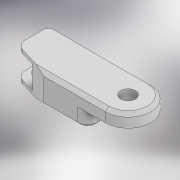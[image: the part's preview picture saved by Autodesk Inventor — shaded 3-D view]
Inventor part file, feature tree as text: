
AUTODESK INVENTOR PART (.ipt)
format: ipt  version: 2022 (Build 260153000, 153)  size: 258,048 bytes
history: native  units: mm
features: extrude x9, sketch x8, projected_geometry x6, fillet x3, chamfer x3
ambient origin geometry x8: Origin, YZ Plane, XZ Plane, XY Plane, X Axis, Y Axis, Z Axis, Center Point
bodies: Solid1 (feature_tree)
feature tree (29):
  sketch  "Sketch2"  dims[d0=4.4mm d1=13.5mm]
  extrude  "Extrusion1"  Depth=13.5mm
  extrude  "Extrusion2"  Depth=8.85mm TaperAngle=0.0deg
  extrude  "Extrusion3"  Depth=1.0mm
  extrude  "Extrusion4"  Depth=8.85mm TaperAngle=0.0deg
  extrude  "Extrusion5"  Depth=8.0mm TaperAngle=0.0deg
  extrude  "Extrusion6"  Depth=8.0mm TaperAngle=0.0deg
  extrude  "Extrusion7"  Depth=3.0mm TaperAngle=0.0deg
  sketch  "Sketch8"  dims[d17=10.25mm d18=0.0mm d19=10.25mm d20=0.0mm d21=3.0mm d22=2.0mm d23=2.0mm d24=45.0deg d25=2.0mm d26=2.0mm d27=45.0deg d28=3.0mm]
  fillet  "Fillet1"  Radius=3.0mm
  chamfer  "Chamfer1"  Distance=2.0mm Angle=45.0deg
  chamfer  "Chamfer2"  Distance=2.0mm Angle=45.0deg
  fillet  "Fillet2"  Radius=3.0mm
  sketch  "Sketch9"  dims[d32=3.85mm d33=0.0mm d34=10.0mm d35=0.0mm d36=1.0mm d37=2.0mm d38=45.0deg d39=1.0mm]
  extrude  "Extrusion8"  Depth=10.0mm TaperAngle=0.0deg
  extrude  "Extrusion9"  Depth=1.0mm TaperAngle=45.0deg
  chamfer  "Chamfer4"  Distance=1.0mm
  fillet  "Fillet3"  [1 undecoded]
  sketch  "Sketch3"  dims[d2=3.85mm d3=0.0mm d4=8.85mm d5=0.0mm]
  projected_geometry  "Projected Loop1"
  sketch  "Sketch4"  dims[d6=0.5mm d7=1.0mm]
  projected_geometry  "Projected Loop2"
  sketch  "Sketch5"  dims[d8=12.5mm d9=8.85mm d10=0.0mm]
  projected_geometry  "Projected Loop3"
  sketch  "Sketch6"  dims[d11=1.0mm d12=8.0mm d13=0.0mm]
  sketch  "Sketch7"  dims[d14=5.1mm d15=8.0mm d16=0.0mm]
  projected_geometry  "Projected Loop5"
  projected_geometry  "Projected Loop6"
  projected_geometry  "Projected Loop7"
note: 1 required parameter value undecoded (feature->parameter linkage not recoverable at this tier; creation-order binding heuristic only, values carry confidence <= 0.55)
